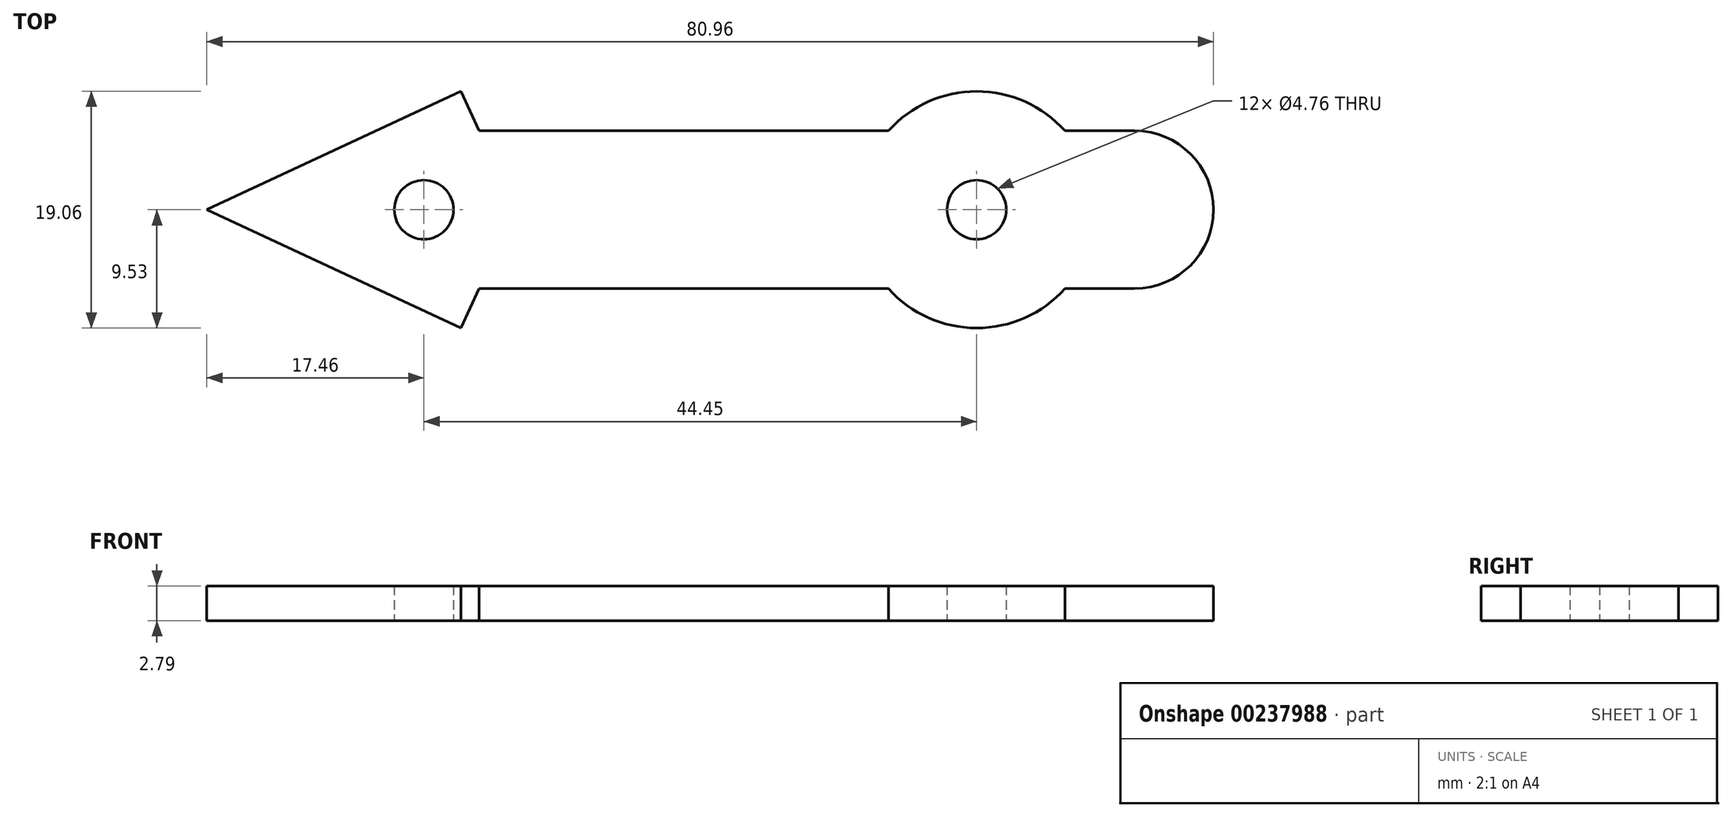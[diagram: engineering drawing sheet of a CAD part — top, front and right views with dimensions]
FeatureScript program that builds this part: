
annotation { "Feature Type Name" : "Feature", "Feature Type Description" : "" }
export const myFeature = defineFeature(function(context is Context, id is Id, definition is map)
    precondition{}
    {
        {
            var Q0;
            Q0=qCreatedBy(makeId("Top.planeOp"),FACE);
            var sketch = newSketch(context, id + "F0", { "sketchPlane" : qUnion([Q0])});
            skLineSegment(sketch, "E0.bottom", {"start": v(-6.35, 6.35) * mm, "end": v(-59.06, 6.35) * mm});
            skLineSegment(sketch, "E0.top", {"start": v(-6.35, -6.35) * mm, "end": v(-59.06, -6.35) * mm});
            skLineSegment(sketch, "E0.right", {"start": v(-59.06, 6.35) * mm, "end": v(-59.06, -6.35) * mm});
            skLineSegment(sketch, "E1", {"start": v(-59.06, 6.35) * mm, "end": v(-60.54, 9.53) * mm});
            skLineSegment(sketch, "E2", {"start": v(-60.54, 9.53) * mm, "end": v(-80.96, 0) * mm});
            skLineSegment(sketch, "E3", {"start": v(-80.96, 0) * mm, "end": v(-60.54, -9.53) * mm});
            skLineSegment(sketch, "E4", {"start": v(-60.54, -9.53) * mm, "end": v(-59.06, -6.35) * mm});
            skLineSegment(sketch, "E5", {"start": v(0, 0) * mm, "end": v(-80.96, 0) * mm, "construction": true});
            skCircle(sketch, "E6", {"center": v(-19.05, 0) * mm, "radius": 2.38 * mm});
            skCircle(sketch, "E7", {"center": v(-63.5, 0) * mm, "radius": 2.38 * mm});
            skPoint(sketch, "E8.orphan", {"position": v(0, 6.35) * mm});
            skPoint(sketch, "E9.orphan", {"position": v(0, -6.35) * mm});
            skArc(sketch, "E10", {"start": v(-6.35, 6.35) * mm, "mid": v(0, 0) * mm, "end": v(-6.35, -6.35) * mm});
            skCircle(sketch, "E11", {"center": v(-19.05, 0) * mm, "radius": 9.53 * mm});
            skSolve(sketch);
        }
        {
            var Q0;
            Q0 = qSketchRegion(id + "F0", true);
            extrude(context, id + "F1", {"entities" : qUnion([Q0]), "depth" : 2.8 * mm});
        }
    });
